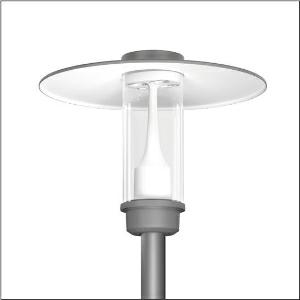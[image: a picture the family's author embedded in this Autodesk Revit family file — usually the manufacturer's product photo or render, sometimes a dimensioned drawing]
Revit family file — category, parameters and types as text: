
# Revit family: litepole_2_iq___st1_2a_5xa5425kf14h_4f30
name_source: partatom
category: Lighting Fixtures
units: mm (PartAtom-declared; Revit-internal decimal feet)

## family parameters
Cut with Voids When Loaded = No
Host = Face
Light Source = No
Part Type = Normal
Room Calculation Point = No
Round Connector Dimension = Use Diameter
Shared = No

## types (1)
- --- (1 x LED, 1550 lm, 10 W, 4000K)
    Apparent Load = 10 VA
    CIE Flux Codes = 22 60 92 98 100
    Color Rendering = 70
    Color Temperature = 4000K
    Default Elevation = 1800 mm
    Description = Litepole 2 iQ, mast luminaire, Module 540 iQ-SR, primary light control with 3 zone facetted reflector, of plastic, silver coated, highly specular, structured, primary optical cover: cover, of PMMA, transparent, light distribution: ST1.2a, light emission: direct distribution, primary light characteristic: asymmetric, installation type: post-top, LED, High Power LED, rated luminous flux: 1.550lm, luminous efficacy: 155lm/W, light colour: 740, colour temperature: 4000K, control gear: iQ Street-Remote, control: pre-setting: logarithmic dimming characteristic, Street-Remote, Auto-Match, Temp-Guard, Lumen-Switch, Night-Set, Smart-Wire, Light-Fading, Desk-Remote (wireless, voltage-free reading and setting of iQ features in the workshop via application-optimized NFC function/RFID function), optimised constant luminous flux control (CLO 2.0), with terminal, 6-pole, max. 2.5mm², mains connection: 230..240V, AC, 50/60Hz, start of lifetime: 10W, end of service life: 10W, reduction: 5W, luminaire housing, upper part, of aluminium, coated, Siteco® metallic grey (DB 702S), diameter: 750mm, height: 590mm, spigot size: d x l = 76 x 70mm (post-top) | with reducer (optional accessory) 60 x 70mm, mounting height: 3..5m, post-top mast mounting element, of diecast aluminium, coated, Siteco® metallic grey (DB 702S), Module 540 iQ-SR, traffic white (RAL 9016), equipment: standard, protection rating (complete): IP65, insulation class (complete): insulation class II (safety insulation), certification: CE, ENEC, VDE, packaging unit: 1 piece

Light Distribution: ST1.2a
    Height = 590 mm
    Lamp = 1 x LED
    Lamp Light Flux = 1550 lm
    Lamp Power = 10 W
    Lamp count = 1
    Length = 750 mm
    Luminous efficacy = 155 lm/W
    Manufacturer = Siteco
    ModVariant = No
    Model = 5XA5425KF14H
    Number of Poles = 1
    OnlyDefault = Yes
    Power Factor = 1
    Product Name = Litepole 2 iQ | ST1.2a
    Product group = mast luminaire | pylon top
    ProductGroupID = 6100
    Protection Class = Protection class II
    Protection Degree = IP 65
    RLX_Detail_Level = 1
    RLX_Emergency_Light_Flux = 0 lm
    RLX_Emergency_Type = 0
    RLX_Emergency_Type_DB = No
    RlxData = <blob elided: 67993 chars, md5=f5a6af80>
    Socket = socket
    Standby Power = 0 W
    System Light Flux = 1550 lm
    System Power = 10 W
    Type Comments = factory setting: luminous flux: 100 % | dim-lin: 254 | 401 mA
    Type Image = l_1006518.jpg
    URL = http://relux.com
    VarID = @adj_193857
    Voltage = 0 V
    Weight = 0.00 kg
    Width = 0 mm  [stored 0 ft]

note: [stored X ft] marks values corroborated as IEEE doubles in the binary element streams (Revit-internal decimal feet)

## geometry (parser evidence)
native form markers: Blend x4, Sweep x11
no freeform markers — native parametric forms only
